# Revit family: Electrical_Equipment-Floor_Box-Hubbell_Wiring-1_Gang-Rectangular_Cast_Iron-B2436
name_source: partatom
category: Electrical Fixtures
revit_build: Autodesk Revit 2015 (Build: 20140606_1530(x64)
units: mm (PartAtom-declared; Revit-internal decimal feet)

## types (3) — shared parameters
Assembly Code = D5020115
Box Material = Metal-Hubbell-Cast Iron
Default Elevation = 0' - 0"
Description = Flush Rectangular Cast Iron Concrete Floor Box
Manufacturer = Hubbell-Wiring
Product Documentation Link = http://ecatalog.hubbell-wiring.com
Product Page URL = http://ecatalog.hubbell-wiring.com
Product data url = https://bimobject.com
URL = http://www.hubbell-wiring.com

## per-type parameters (varying)
| type | Collar Material | Conduit Connector 1 Radius | Conduit Connector_1 Description | Conduit Connector_2 Description | Conduit Connector_3 Description | Conduit Connector_4 Description | Floor Box Type | Model |
| B2436 - 1 Gang - Brass Collar | Metal-Hubbell-Brass | 0' - 0 3/8" | Conduit 0.75in. Connection | Conduit 0.75in. Connection | Conduit 0.75in. Connection | Conduit 0.75in. Connection | Cast Iron Concrete Floor Box : B2436 - Deep Concrete Floor Box | B2436 |
| BA2436 - 1 Gang - Aluminum Collar | Metal-Hubbell-Aluminum | 0' - 0 3/8" | Conduit 0.75in. Connection | Conduit 0.75in. Connection | Conduit 0.75in. Connection | Conduit 0.75in. Connection | Cast Iron Concrete Floor Box : BA2436 - Deep Concrete Floor Box | BA2436 |
| B243641 - 1 Gang - Brass Collar | Metal-Hubbell-Brass | 0' - 0 1/2" | Conduit 1.0in. Connection | Conduit 1.0in. Connection | Conduit 1.0in. Connection | Conduit 1.0in. Connection | Cast Iron Concrete Floor Box : B243641 - Deep Concrete Floor Box | B243641 |

## geometry (parser evidence)
native form markers: Blend x22, Sweep x8
no freeform markers — native parametric forms only
